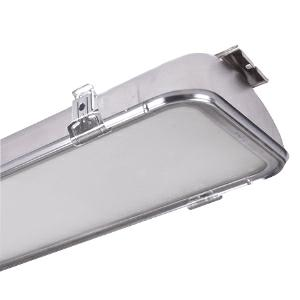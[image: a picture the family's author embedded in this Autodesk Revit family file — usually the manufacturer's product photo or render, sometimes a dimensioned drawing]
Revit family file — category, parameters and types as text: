
# Revit family: 3f_filippi_-_beta_235_93_vs_ampio_3f_filippi_-_52881_-_beta_235_led_932x40_ampio_vs_l1265
name_source: partatom
category: Lighting Fixtures
units: mm (PartAtom-declared; Revit-internal decimal feet)

## family parameters
Cut with Voids When Loaded = No
Host = Face
Light Source = No
Part Type = Normal
Room Calculation Point = No
Round Connector Dimension = Use Diameter
Shared = No

## types (1)
- 3F Filippi - Beta 235 93 VS Ampio (1 x LED, 11449 lm, 80 W, 4000 K)
    Apparent Load = 80 VA
    Approval mark = CE
    CIE Flux Codes = 65 90 98 100 100
    Color Rendering = 80
    Color Temperature = 4000 K
    Control Gear = Electronic ballast
    Default Elevation = 1800 mm
    Description = ILLUMINOTECHNICAL
Luminous efficiency 100% (DLOR 100%, ULOR 0%).
Initial luminous flux of the luminaire 11449 lm.
Wide symmetric distribution.
Installation Interdistance Transv.D = 1.26 x hu - Long.D = 1.32 x hu.
Tabular UGR (CIE 117 - 4H-8H; S=0.25H; 70/50/20): RUG 21.4 - 22.5.
Beam angle: 87° - 92°.
Luminous efficacy 143 lm/W.
Lifetime (L93/B10): 30000 h. (tq+25°C)
Lifetime (L90/B10): 50000 h. (tq+25°C)
Lifetime (L85/B10): 80000 h. (tq+25°C)
Lifetime (L80/B10): 100000 h. (tq+25°C)
Lifetime (L85/B10): 50000 h. (tq+45°C)
Sudden decreased luminous flux after 50000 hours: 0% (C0).
Photobiological safety in compliance with IEC/TR 62778: RG0 risk exempt, (IEC 62471).
In compliance with IEC/EN 62722-2-1 - IEC/EN 62717 standards.

SOURCE
2 linear LED modules 40W/840.
Energy efficiency class (UE 2019/2020 - UE 2019/2015): C.
CIE 13.3 Colour rendering index: CRI >80 (R9 <50%).
IES TM-30 Fidelity Index: Rf = 84 Rg = 95.
CCT nominal colour temperature 4000 K.
Colour initial tolerance (MacAdam): SDCM 3.

MECHANICAL
Housing in AISI 304 stainless steel, pressed in one single piece.
VS moulded anti-glare glass, non-combustible, single-piece perimeter frame in stainless steel.
Oversized gear-tray reflector unit in highly reflective white painted hot-galvanised steel.
Methacrylate (PMMA) lenses with external flat surface.
Stainless steel snap-lock clips for diffuser mounting (safety n° 4 per fixture).
Luminaire with limited surface temperature. - D - (EN 60598-2-24)
Dimensions: 1265x235 mm, height 105 mm. Weight 9.375 kg.
IP65 protection degree.
Mechanical strength to impacts IK09 (10 joule).
Glow-wire test resistance 960°C.

ELECTRICAL
Halogen Free electronic wiring 230V-50/60Hz, power factor 0.95, THD <25%, constant output current, class I, 1 driver.
Power of the luminaire 80 W.
ENEC - CE.
Flicker: <4%.
Luminaire compliant with EN 60598-2-22 for power supply from a centralised emergency system CPSS (Central Power Supply System), not incorporated in the luminaire - high risk areas excluded. The default power and flux are 100% in AC and 100% in DC.
Ambient temperature from -20°C to +45°C.
Temperature class T6 max 85°C.
Quick connection via M20 3P connector with 9-13 mm tightening range.
Relative humidity UR: <85%.

INSTALLATION
Ceiling / Suspended / Wall.
All accessories dedicated to this product are available on the Catalog and on our website www.3F-Filippi.com.

APPLICATIONS
Dry, dusty indoor environments, subject to occasional water splashes.
Any environments except the ones where the luminaire materials are unsuitable.
Industrial environments, warehouses, environments where security locks are required on all clips, e.g. prisons (on request).
Environments in which it is necessary a total protection against falling fragments (eg environments with foodstuffs or machines with moving parts or with extreme temperature changes), use luminaires with laminated glass.
Tempered glass is not immune to falling fragments from harmless and caused by shocks or exceptionally derived from the tempering process.

WARNING
Fixture not suitable for cold stores with an ambient temperature <0°C and/or relative humidity >85%.
Luminaire designed for disposal/recycling at end-of-life.
Replaceable (LED only) light source by a professional. Replaceable control gear by a professional.
    Height = 105 mm
    Lamp = 1 x LED
    Lamp Light Flux = 11449 lm
    Lamp Power = 80 W
    Lamp count = 1
    Length = 1265 mm
    Lifetime = 50000 h
    Luminous efficacy = 143 lm/W
    Manufacturer = 3F Filippi
    ModVariant = No
    Model = 3F Filippi - 52881 - Beta 235 LED 932x40 AMPIO VS L1265
    Mounting Place = Ceiling
    Mounting Type = Pendant
    Number of Poles = 1
    OnlyDefault = Yes
    Power Factor = 1
    Product Name = 3F Filippi - Beta 235 93 VS Ampio
    Product group = pendant luminaire
    ProductGroupID = 9
    Protection Class = Protection class I
    Protection Degree = IP 65
    RLX_Detail_Level = 1
    RLX_Emergency_Light_Flux = 0 lm
    RLX_Emergency_Type = 0
    RLX_Emergency_Type_DB = No
    RlxData = <blob elided: 83325 chars, md5=9ae0a0d3>
    Socket = socket
    Standby Power = 0 W
    System Light Flux = 11449 lm
    System Power = 80 W
    Type Comments = Product without accessories
    Type Image = 3ffilippi_52881.jpg
    URL = http://relux.com
    VarID = ---
    Voltage = 0 V
    Weight = 0.00 kg
    Width = 235 mm

## geometry (parser evidence)
native form markers: Blend x4, Sweep x11
no freeform markers — native parametric forms only
